# Revit family: 11-HC_RAS_HCL_TOSHIBA_TCTC_3MU2VAG_18
name_source: partatom
category: Mechanical Equipment
revit_build: Autodesk Revit 2017 (Build: 20160225_1515(x64)
units: mm (PartAtom-declared; Revit-internal decimal feet)

## family parameters
Always vertical = Yes
Cut with Voids When Loaded = No
OmniClass Number = 23.75.00.00
OmniClass Title = Climate Control (HVAC)
Part Type = Normal
Room Calculation Point = No
Round Connector Dimension = Use Diameter
Shared = No
Work Plane-Based = No

## types (1)
- RAS-3M18U2AVG-E
    Airflow m3/h- Cooling/Heating = 2177 / 2077
    Article Description = Multi R32
    Article Type = RAS-3M18U2AVG-E
    Compressor Type = Hermetic DC Twin rotary compressor
    Compressor detail - Motor output  (kW) = 1320
    Content Supplier URL = www.hcltech.com
    Custom = No
    Depth (mm) = 300 mm
    Description = Multi R32
    Drain pipe = -
    Duct diameters = -
    EMCS = 4
    ETIM Article Class = EC001213
    Energy class = A++ / A++
    Frequency (Hz) = 50Hz
    Height (mm) = 630 mm  [stored 2.06693 ft]
    Hydronic Return Diameter (mm) = 10 mm  [stored 0.0328084 ft]
    Hydronic Supply Diameter (mm) = 6 mm  [stored 0.019685 ft]
    MEPcontent Class = HEATPUMP
    MOCP (A) = 15
    Manufacturer = Toshiba
    Manufacturer Art. No. = RAS-3M18U2AVG-E
    Manufacturer URL = https://www.toshiba-carrier.co.jp
    Model = RAS-3M18U2AVG-E
    Operating range - Cooling (°C) = -10 - 46
    Operating range - Heating (°C) = -20 - 24
    Pdesigh = 7.5 / 5.2
    Power consumption-Cooling (Kw) = 1170
    Power consumption-Heating (Kw) = 1580
    Product Line = TCTC
    Rated Capacity kW - Cooling/Heating = 5.2 / 6.8
    Rated Power Consumption kW - Cooling/Heating = 1170 / 1580
    Rated efficiency - EER / COP = 4.44 / 4.30
    Red = Colour RGB-250 000 000
    Refrigerant information = R32
    Running current-Cooling (A) = 5.64/5.39/5.17
    Running current-Heating (A) = 7.54/7.22/6.92
    Seasonal efficiency - SEER  / SCOP = 6.80 / 4.60
    Sound pressure dB(A) Cooling/Heating- High = 47 / 50
    Starting current = 5.64
    URL = https://www.toshiba-carrier.co.jp
    Voltage (V) = 220-240V
    Weight (Kg) = 46
    White = Colour RGB-255 255 255
    Width (mm) = 799 mm  [stored 2.62139 ft]

note: [stored X ft] marks values corroborated as IEEE doubles in the binary element streams (Revit-internal decimal feet)

## geometry (parser evidence)
native form markers: Sweep x7
no freeform markers — native parametric forms only
